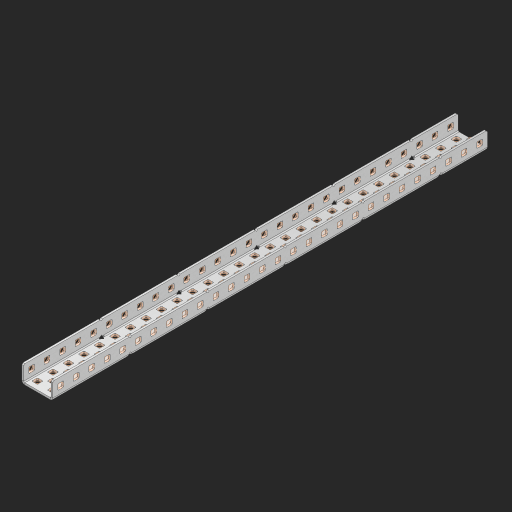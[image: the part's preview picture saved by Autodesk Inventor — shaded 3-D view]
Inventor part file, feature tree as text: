
AUTODESK INVENTOR PART (.ipt)
format: ipt  version: 2023 (Build 270158000, 158)  size: 1,748,480 bytes
history: native  units: in
note: dims shown in document units (in); Inventor stores cm internally (conversion verified against a paired STEP export)
features: other x147, extrude x138, sheet_metal_op x11, sketch x10, pattern_linear x2, mirror x1, chamfer x1
ambient origin geometry x8: Origin, YZ Plane, XZ Plane, XY Plane, X Axis, Y Axis, Z Axis, Center Point
bodies: Solid1 (feature_tree), Body (feature_tree)
feature tree (310):
  sheet_metal_op  "Flanges"
  other  "Flange Pattern Plane"
  other  "Flange Pattern Sketch"
  sheet_metal_op  "Flange Pattern"
  sheet_metal_op  "Body Pattern"
  pattern_linear  "Center Pattern"  Spacing1=0.0625in  [1 undecoded]
  other  "Arc Length"
  mirror  "Notch Mirror"
  pattern_linear  "Notch Pattern"  Spacing1=0.182in  [1 undecoded]
  chamfer  "End Chamfer"
  extrude  "Half Cut"  Depth=0.02in
  sketch  "Sketch1"  dims[d0=1.0in]
  other  "Plate1"
  sketch  "Sketch2"  dims[d1=14.0in]
  other  "Plate2"
  sheet_metal_op  "Bend1"
  sheet_metal_op  "Corner1"
  sketch  "Sketch3"  dims[d2=0.0625in]
  sketch  "Sketch7"  dims[d3=0.0625in]
  other  "Srf1"
  other  "Srf2"
  sketch  "Sketch8"  dims[d4=0.0312in]
  sketch  "Sketch9"  dims[d5=0.125in]
  other  "Srf91"
  sheet_metal_op  "Body Pattern Sketch"
  other  "Srf92"
  sketch  "Sketch13"  dims[d6=0.0625in]
  sketch  "Sketch14"  dims[d7=0.5in d8=90.0deg d9=0.0312in]
  sketch  "Sketch15"  dims[d10=0.25in]
  sketch  "Sketch16"  dims[d11=0.0625in d12=0.0625in d16=0.182in d17=0.02in d18=0.0625in d19=0.0in d20=0.25in d21=0.25in d38=11.0236in d40=0.5in d41=0.7874in d43=1.0in d46=0.172in d47=1.0in d48=0.0in d49=0.182in d50=0.02in d51=0.25in d52=0.25in d53=0.0625in d54=0.0in d55=0.172in d56=1.0in d57=0.0in d58=0.25in d60=11.0236in d62=0.5in d63=0.7874in d65=0.5in d85=0.1473in d86=0.1782in d88=0.04in d89=0.0625in d90=0.0in d91=0.04in d92=0.0491in d95=2.5in d96=0.04in d97=0.25in d98=45.0deg d99=0.25in d100=0.5in d101=0.0in d102=2.497in d106=0.182in d107=0.02in d108=0.5in d109=0.5in d110=0.0625in d111=0.0in d112=0.172in d113=0.5in d114=0.0in d117=0.5in d118=0.5in d119=0.5in]
  other  "Srf786"
  other  "Srf823"
  other  "Srf824"
  other  "Srf825"
  other  "Srf826"
  other  "Srf827"
  other  "Srf828"
  other  "Srf829"
  other  "Srf856"
  other  "Srf857"
  other  "Srf858"
  other  "Srf859"
  other  "Srf860"
  other  "Srf861"
  other  "Srf862"
  other  "Srf889"
  other  "Srf890"
  other  "Srf891"
  other  "Srf892"
  other  "Srf893"
  other  "Srf894"
  other  "Srf895"
  other  "Srf896"
  other  "Srf922"
  other  "Srf923"
  other  "Srf924"
  other  "Srf925"
  other  "Srf926"
  other  "Srf959"
  other  "Srf960"
  other  "Srf961"
  other  "Srf962"
  other  "Srf963"
  other  "Srf996"
  other  "Srf997"
  other  "Srf998"
  other  "Srf999"
  other  "Srf1000"
  other  "Srf1143"
  other  "Srf1144"
  other  "Srf1145"
  other  "Srf1146"
  other  "Srf1147"
  other  "Srf1148"
  other  "Srf1149"
  other  "Srf1150"
  other  "Srf1151"
  other  "Srf1152"
  other  "Srf1153"
  other  "Srf1154"
  other  "Srf1155"
  other  "Srf1156"
  other  "Srf1157"
  other  "Srf1158"
  other  "Srf1159"
  other  "Srf1160"
  other  "Srf1161"
  other  "Srf1162"
  other  "Srf1163"
  other  "Srf1164"
  other  "Srf1165"
  other  "Srf1166"
  other  "Srf1167"
  other  "Srf1168"
  other  "Srf1169"
  other  "Srf1170"
  other  "Srf1171"
  other  "Srf1172"
  other  "Srf1173"
  other  "Srf1174"
  other  "Srf1175"
  other  "Srf1176"
  other  "Srf1177"
  other  "Srf1178"
  other  "Srf1179"
  other  "Srf1180"
  other  "Srf1181"
  other  "Srf1182"
  other  "Srf1183"
  other  "Srf1184"
  other  "Srf1199"
  other  "Srf1200"
  other  "Srf1201"
  other  "Srf1202"
  other  "Srf1203"
  other  "Srf1204"
  other  "Srf1205"
  other  "Srf1206"
  other  "Srf1207"
  other  "Srf1208"
  other  "Srf1209"
  other  "Srf1210"
  other  "Srf1211"
  other  "Srf1212"
  other  "Srf1213"
  other  "Srf1214"
  other  "Srf1215"
  other  "Srf1216"
  other  "Srf1217"
  other  "Srf1218"
  other  "Srf1219"
  other  "Srf1220"
  other  "Srf1221"
  other  "Srf1222"
  other  "Srf1223"
  other  "Srf1224"
  other  "Srf1225"
  other  "Srf1226"
  other  "Srf1227"
  other  "Srf1228"
  other  "Srf1229"
  other  "Srf1230"
  other  "Srf1231"
  other  "Srf1232"
  other  "Srf1233"
  other  "Srf1234"
  other  "Srf1235"
  other  "Srf1236"
  other  "Srf1237"
  other  "Srf1238"
  other  "Srf1239"
  other  "Srf1240"
  other  "Srf1255"
  other  "Srf1256"
  other  "Srf1257"
  other  "Srf1258"
  other  "Srf1259"
  other  "Srf1260"
  other  "Srf1261"
  other  "Srf1262"
  other  "Srf1263"
  other  "Srf1264"
  other  "Srf1265"
  other  "Srf1266"
  other  "Srf1267"
  other  "Srf1268"
  sheet_metal_op  "Flange Stamp"
  sheet_metal_op  "Flange Circle"
  sheet_metal_op  "Body Stamp"
  sheet_metal_op  "Body Circle"
  other  "Center Stamp"
  other  "Center Circle"
  sheet_metal_op  "Notch"
  extrude  "ExtrusionSrf2"  Depth=0.0625in
  extrude  "ExtrusionSrf92"  TaperAngle=0.0deg  [1 undecoded]
  extrude  "ExtrusionSrf823"  Depth=0.5in
  extrude  "ExtrusionSrf824"  Depth=0.5in
  extrude  "ExtrusionSrf825"  Depth=0.5in
  extrude  "ExtrusionSrf826"  Depth=0.5in
  extrude  "ExtrusionSrf827"  Depth=1.0in TaperAngle=0.0deg
  extrude  "ExtrusionSrf828"  Depth=0.5in
  extrude  "ExtrusionSrf829"  Depth=0.02in
  extrude  "ExtrusionSrf856"  Depth=0.5in
  extrude  "ExtrusionSrf857"  Depth=0.5in
  extrude  "ExtrusionSrf858"  Depth=0.0625in
  extrude  "ExtrusionSrf859"  TaperAngle=0.0deg  [1 undecoded]
  extrude  "ExtrusionSrf860"  Depth=0.5in
  extrude  "ExtrusionSrf861"  Depth=1.0in TaperAngle=0.0deg
  extrude  "ExtrusionSrf862"  Depth=0.5in
  extrude  "ExtrusionSrf889"  Depth=0.5in
  extrude  "ExtrusionSrf890"  Depth=0.5in
  extrude  "ExtrusionSrf891"  Depth=0.5in
  extrude  "ExtrusionSrf892"  Depth=0.5in
  extrude  "ExtrusionSrf893"  Depth=0.5in
  extrude  "ExtrusionSrf894"  Depth=0.0625in
  extrude  "ExtrusionSrf895"  TaperAngle=0.0deg  [1 undecoded]
  extrude  "ExtrusionSrf896"  Depth=0.5in
  extrude  "ExtrusionSrf922"  Depth=0.5in
  extrude  "ExtrusionSrf923"  Depth=2.5in
  extrude  "ExtrusionSrf924"  Depth=0.5in TaperAngle=45.0deg
  extrude  "ExtrusionSrf925"  Depth=0.5in
  extrude  "ExtrusionSrf926"  Depth=0.5in TaperAngle=0.0deg
  extrude  "ExtrusionSrf959"  Depth=0.5in
  extrude  "ExtrusionSrf960"  Depth=0.5in
  extrude  "ExtrusionSrf961"  Depth=0.02in
  extrude  "ExtrusionSrf962"  Depth=0.5in
  extrude  "ExtrusionSrf963"  Depth=0.5in
  extrude  "ExtrusionSrf996"  Depth=0.0625in
  extrude  "ExtrusionSrf997"  TaperAngle=0.0deg  [1 undecoded]
  extrude  "ExtrusionSrf998"  Depth=0.5in
  extrude  "ExtrusionSrf999"  Depth=0.5in TaperAngle=0.0deg
  extrude  "ExtrusionSrf1000"  Depth=0.5in
  extrude  "ExtrusionSrf1143"  Depth=0.5in
  extrude  "ExtrusionSrf1144"  Depth=0.5in
  extrude  "ExtrusionSrf1145"  [1 undecoded]
  extrude  "ExtrusionSrf1146"  [1 undecoded]
  extrude  "ExtrusionSrf1147"  [1 undecoded]
  extrude  "ExtrusionSrf1148"  [1 undecoded]
  extrude  "ExtrusionSrf1149"  [1 undecoded]
  extrude  "ExtrusionSrf1150"  [1 undecoded]
  extrude  "ExtrusionSrf1151"  [1 undecoded]
  extrude  "ExtrusionSrf1152"  [1 undecoded]
  extrude  "ExtrusionSrf1153"  [1 undecoded]
  extrude  "ExtrusionSrf1154"  [1 undecoded]
  extrude  "ExtrusionSrf1155"  [1 undecoded]
  extrude  "ExtrusionSrf1156"  [1 undecoded]
  extrude  "ExtrusionSrf1157"  [1 undecoded]
  extrude  "ExtrusionSrf1158"  [1 undecoded]
  extrude  "ExtrusionSrf1159"  [1 undecoded]
  extrude  "ExtrusionSrf1160"  [1 undecoded]
  extrude  "ExtrusionSrf1161"  [1 undecoded]
  extrude  "ExtrusionSrf1162"  [1 undecoded]
  extrude  "ExtrusionSrf1163"  [1 undecoded]
  extrude  "ExtrusionSrf1164"  [1 undecoded]
  extrude  "ExtrusionSrf1165"  [1 undecoded]
  extrude  "ExtrusionSrf1166"  [1 undecoded]
  extrude  "ExtrusionSrf1167"  [1 undecoded]
  extrude  "ExtrusionSrf1168"  [1 undecoded]
  extrude  "ExtrusionSrf1169"  [1 undecoded]
  extrude  "ExtrusionSrf1170"  [1 undecoded]
  extrude  "ExtrusionSrf1171"  [1 undecoded]
  extrude  "ExtrusionSrf1172"  [1 undecoded]
  extrude  "ExtrusionSrf1173"  [1 undecoded]
  extrude  "ExtrusionSrf1174"  [1 undecoded]
  extrude  "ExtrusionSrf1175"  [1 undecoded]
  extrude  "ExtrusionSrf1176"  [1 undecoded]
  extrude  "ExtrusionSrf1177"  [1 undecoded]
  extrude  "ExtrusionSrf1178"  [1 undecoded]
  extrude  "ExtrusionSrf1179"  [1 undecoded]
  extrude  "ExtrusionSrf1180"  [1 undecoded]
  extrude  "ExtrusionSrf1181"  [1 undecoded]
  extrude  "ExtrusionSrf1182"  [1 undecoded]
  extrude  "ExtrusionSrf1183"  [1 undecoded]
  extrude  "ExtrusionSrf1184"  [1 undecoded]
  extrude  "ExtrusionSrf1199"  [1 undecoded]
  extrude  "ExtrusionSrf1200"  [1 undecoded]
  extrude  "ExtrusionSrf1201"  [1 undecoded]
  extrude  "ExtrusionSrf1202"  [1 undecoded]
  extrude  "ExtrusionSrf1203"  [1 undecoded]
  extrude  "ExtrusionSrf1204"  [1 undecoded]
  extrude  "ExtrusionSrf1205"  [1 undecoded]
  extrude  "ExtrusionSrf1206"  [1 undecoded]
  extrude  "ExtrusionSrf1207"  [1 undecoded]
  extrude  "ExtrusionSrf1208"  [1 undecoded]
  extrude  "ExtrusionSrf1209"  [1 undecoded]
  extrude  "ExtrusionSrf1210"  [1 undecoded]
  extrude  "ExtrusionSrf1211"  [1 undecoded]
  extrude  "ExtrusionSrf1212"  [1 undecoded]
  extrude  "ExtrusionSrf1213"  [1 undecoded]
  extrude  "ExtrusionSrf1214"  [1 undecoded]
  extrude  "ExtrusionSrf1215"  [1 undecoded]
  extrude  "ExtrusionSrf1216"  [1 undecoded]
  extrude  "ExtrusionSrf1217"  [1 undecoded]
  extrude  "ExtrusionSrf1218"  [1 undecoded]
  extrude  "ExtrusionSrf1219"  [1 undecoded]
  extrude  "ExtrusionSrf1220"  [1 undecoded]
  extrude  "ExtrusionSrf1221"  [1 undecoded]
  extrude  "ExtrusionSrf1222"  [1 undecoded]
  extrude  "ExtrusionSrf1223"  [1 undecoded]
  extrude  "ExtrusionSrf1224"  [1 undecoded]
  extrude  "ExtrusionSrf1225"  [1 undecoded]
  extrude  "ExtrusionSrf1226"  [1 undecoded]
  extrude  "ExtrusionSrf1227"  [1 undecoded]
  extrude  "ExtrusionSrf1228"  [1 undecoded]
  extrude  "ExtrusionSrf1229"  [1 undecoded]
  extrude  "ExtrusionSrf1230"  [1 undecoded]
  extrude  "ExtrusionSrf1231"  [1 undecoded]
  extrude  "ExtrusionSrf1232"  [1 undecoded]
  extrude  "ExtrusionSrf1233"  [1 undecoded]
  extrude  "ExtrusionSrf1234"  [1 undecoded]
  extrude  "ExtrusionSrf1235"  [1 undecoded]
  extrude  "ExtrusionSrf1236"  [1 undecoded]
  extrude  "ExtrusionSrf1237"  [1 undecoded]
  extrude  "ExtrusionSrf1238"  [1 undecoded]
  extrude  "ExtrusionSrf1239"  [1 undecoded]
  extrude  "ExtrusionSrf1240"  [1 undecoded]
  extrude  "ExtrusionSrf1255"  [1 undecoded]
  extrude  "ExtrusionSrf1256"  [1 undecoded]
  extrude  "ExtrusionSrf1257"  [1 undecoded]
  extrude  "ExtrusionSrf1258"  [1 undecoded]
  extrude  "ExtrusionSrf1259"  [1 undecoded]
  extrude  "ExtrusionSrf1260"  [1 undecoded]
  extrude  "ExtrusionSrf1261"  [1 undecoded]
  extrude  "ExtrusionSrf1262"  [1 undecoded]
  extrude  "ExtrusionSrf1263"  [1 undecoded]
  extrude  "ExtrusionSrf1264"  [1 undecoded]
  extrude  "ExtrusionSrf1265"  [1 undecoded]
  extrude  "ExtrusionSrf1266"  [1 undecoded]
  extrude  "ExtrusionSrf1267"  [1 undecoded]
  extrude  "ExtrusionSrf1268"  [1 undecoded]
note: 102 required parameter values undecoded (feature->parameter linkage not recoverable at this tier; creation-order binding heuristic only, values carry confidence <= 0.55)
